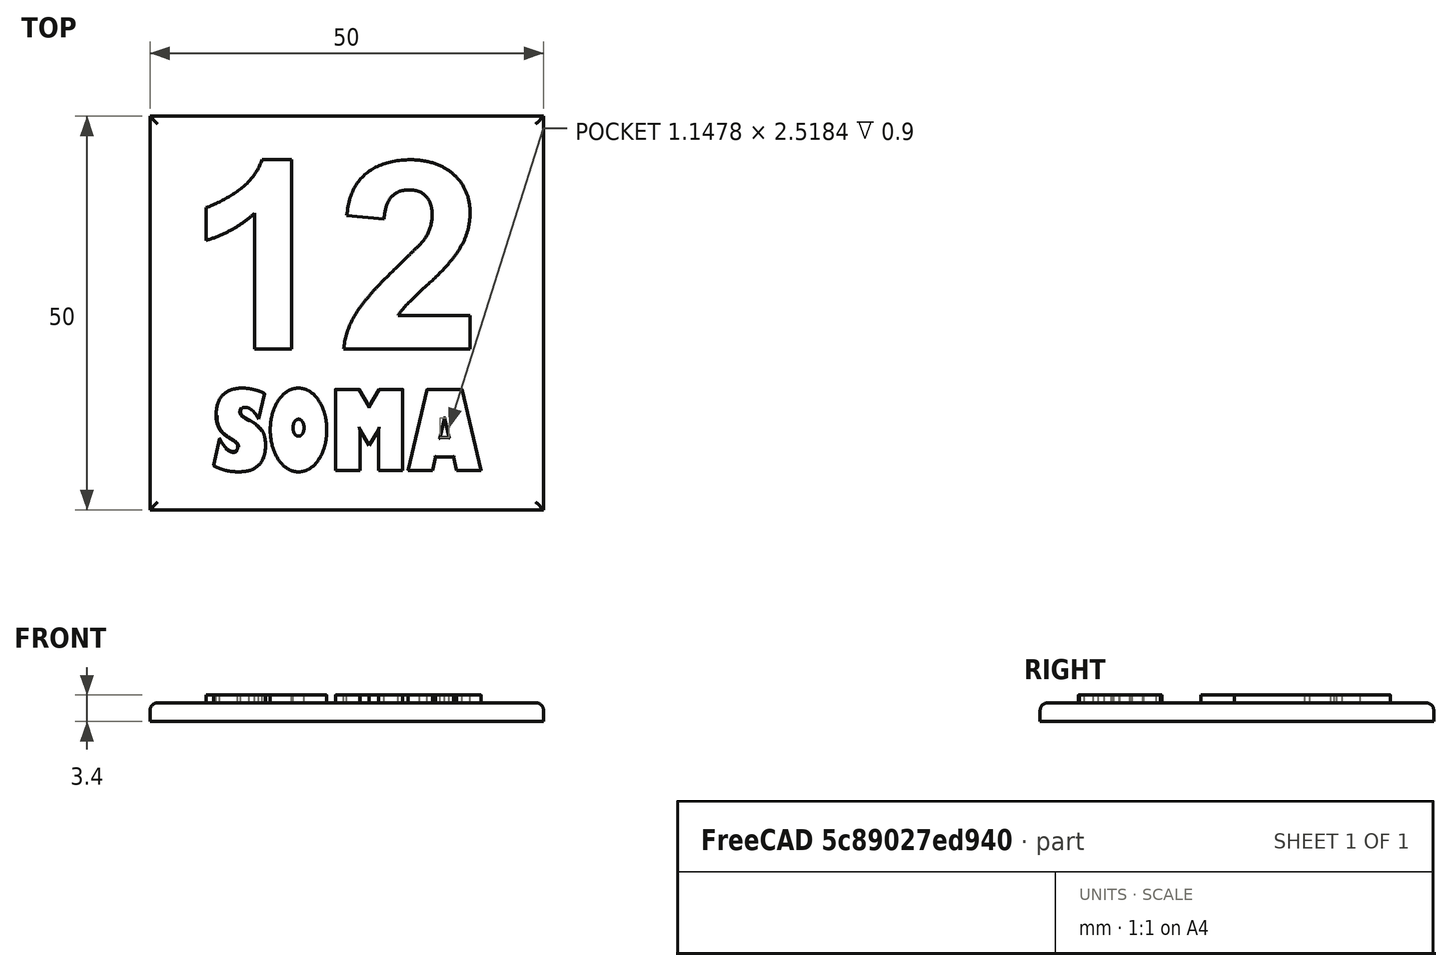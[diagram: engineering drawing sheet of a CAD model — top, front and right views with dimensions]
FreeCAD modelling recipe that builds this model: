
FCSTD DOCUMENT  (FreeCAD 0.21R33771 (Git))
Label: somaNums
License: All rights reserved
LicenseURL: http://en.wikipedia.org/wiki/All_rights_reserved
objects: Part::Part2DObjectPython×2, Part::Extrusion×2, Part::Fillet×2, Part::MultiFuse×2, Part::Box×1
note: 9 computed .brp shape members not serialized (recipe doc carries the construction recipe); baked Part::Feature solids carry a one-line shape summary decoded from their .brp

FEATURE [Part::Box] Box  label="Base"
  AttacherType = Attacher::AttachEngine3D
  Height = 2.4
  Length = 50
  Width = 50
FEATURE [Part::Part2DObjectPython] ShapeString  # Draft 2D object (typed FeaturePython)
  FontFile = <path>
  MakeFace = true
  Placement = pos=(8,5,2.4) rot=(0,0,1;0rad)
  Size = 12
  String = SOMA
  Tracking = 0
FEATURE [Part::Extrusion] Extrude  label="Soma"
  Base = -> ShapeString
  Dir = (0,0,1)
  DirMode = 2
  FaceMakerClass = Part::FaceMakerBullseye
  LengthFwd = 1
  LengthRev = 0
  Solid = true
  Symmetric = false
FEATURE [Part::Part2DObjectPython] ShapeString001  # Draft 2D object (typed FeaturePython)
  FontFile = <path>
  MakeFace = true
  Placement = pos=(4.52,20.41,2.4) rot=(0,0,1;0rad)
  Size = 27
  String = 12
  Tracking = 0
FEATURE [Part::Extrusion] Extrude001
  Base = -> ShapeString001
  Dir = (0,0,1)
  DirMode = 2
  FaceMakerClass = Part::FaceMakerBullseye
  LengthFwd = 1
  LengthRev = 0
  Solid = true
  Symmetric = false
FEATURE [Part::Fillet] Fillet
  Base = -> Box
  Edges = 4 edges r=1: [Edge2,Edge6,Edge10,Edge12]
FEATURE [Part::MultiFuse] Fusion
  Refine = true
  Shapes = -> [Fillet,Extrude001]
FEATURE [Part::Fillet] Fillet001
  Base = -> Extrude
  Edges = 71 edges r=0.1: [Edge4,Edge7,Edge10,Edge13,Edge16,Edge19,Edge22,Edge25,Edge28,Edge31,Edge34,Edge37,Edge40,Edge43,Edge46,Edge49,Edge52,Edge55,Edge58,Edge61,Edge64,Edge67,Edge70,Edge73,Edge76,Edge79,Edge82,Edge84,Edge88,Edge91,Edge94,Edge97,Edge100,Edge103,Edge106,Edge109,Edge112,Edge115,Edge118,Edge120,Edge124,+30 more]
FEATURE [Part::MultiFuse] Fusion001
  Refine = true
  Shapes = -> [Fillet001,Fusion]
note: 2 file-system paths scrubbed to <path> (originals preserved in the JSON sidecar)
